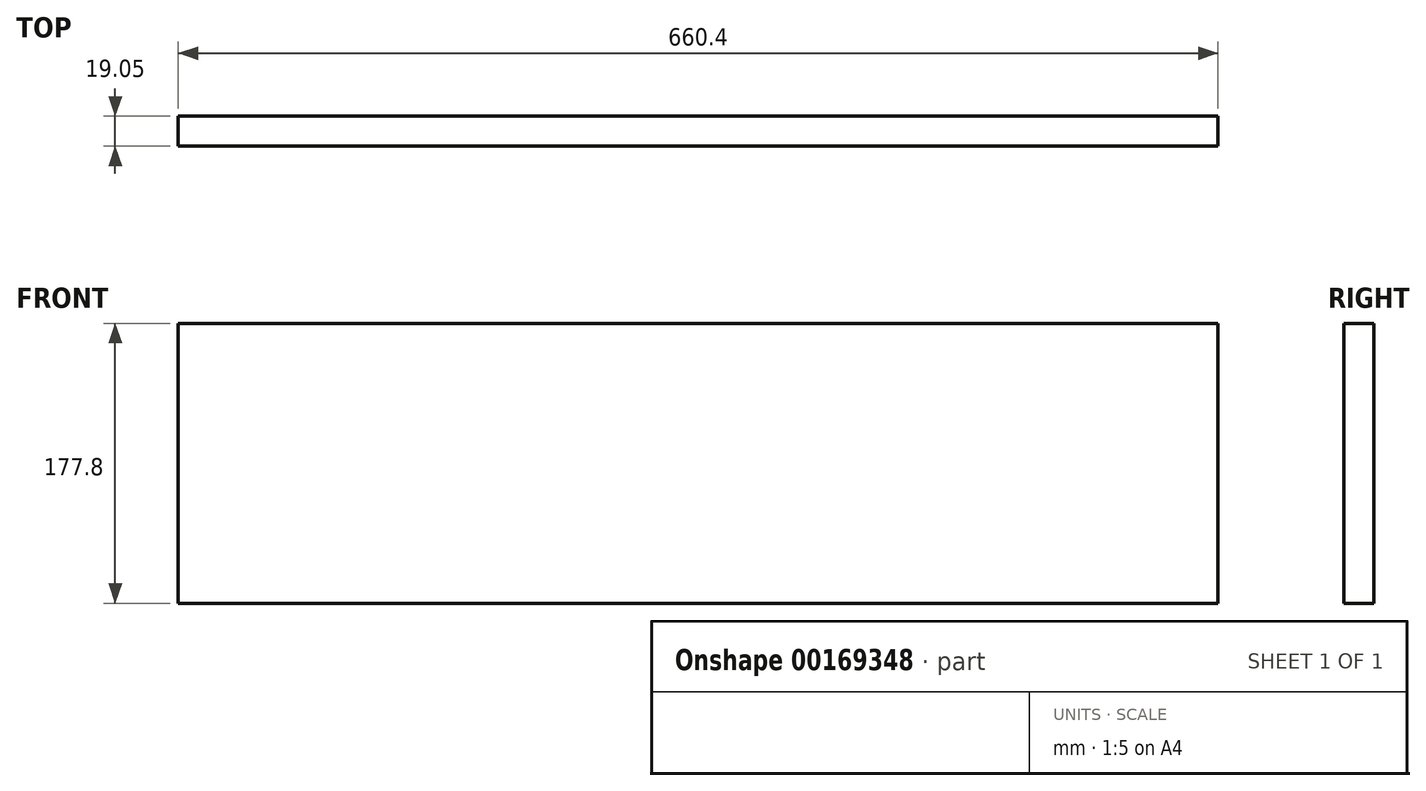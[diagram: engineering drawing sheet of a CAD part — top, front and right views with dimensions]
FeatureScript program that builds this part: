
annotation { "Feature Type Name" : "Feature", "Feature Type Description" : "" }
export const myFeature = defineFeature(function(context is Context, id is Id, definition is map)
    precondition{}
    {
        {
            var Q0;
            Q0=qCreatedBy(makeId("Front.planeOp"),FACE);
            var sketch = newSketch(context, id + "F0", { "sketchPlane" : qUnion([Q0])});
            skLineSegment(sketch, "E0.bottom", {"start": v(0, 0) * mm, "end": v(660.4, 0) * mm});
            skLineSegment(sketch, "E0.top", {"start": v(0, 44.45) * mm, "end": v(660.4, 44.45) * mm});
            skLineSegment(sketch, "E0.left", {"start": v(0, 0) * mm, "end": v(0, 44.45) * mm});
            skLineSegment(sketch, "E0.right", {"start": v(660.4, 0) * mm, "end": v(660.4, 44.45) * mm});
            skLineSegment(sketch, "E1.top", {"start": v(0, 88.9) * mm, "end": v(660.4, 88.9) * mm});
            skLineSegment(sketch, "E1.left", {"start": v(0, 44.45) * mm, "end": v(0, 88.9) * mm});
            skLineSegment(sketch, "E1.right", {"start": v(660.4, 44.45) * mm, "end": v(660.4, 88.9) * mm});
            skLineSegment(sketch, "E2.top", {"start": v(0, 133.35) * mm, "end": v(660.4, 133.35) * mm});
            skLineSegment(sketch, "E2.left", {"start": v(0, 88.9) * mm, "end": v(0, 133.35) * mm});
            skLineSegment(sketch, "E2.right", {"start": v(660.4, 88.9) * mm, "end": v(660.4, 133.35) * mm});
            skLineSegment(sketch, "E3.top", {"start": v(0, 177.8) * mm, "end": v(660.4, 177.8) * mm});
            skLineSegment(sketch, "E3.left", {"start": v(0, 133.35) * mm, "end": v(0, 177.8) * mm});
            skLineSegment(sketch, "E3.right", {"start": v(660.4, 133.35) * mm, "end": v(660.4, 177.8) * mm});
            skSolve(sketch);
        }
        {
            var Q0;
            Q0=makeQuery(id+"F0.imprint","IMPRINT",FACE,{"disambiguationData":[TD([[makeQuery(id+"F0.imprint","IMPRINT",EDGE,{"derivedFrom":sQuery(id+"F0.wireOp",EDGE,"E2.top")}),1.0]])]});
            var Q1;
            Q1=makeQuery(id+"F0.imprint","IMPRINT",FACE,{"disambiguationData":[TD([[makeQuery(id+"F0.imprint","IMPRINT",EDGE,{"derivedFrom":sQuery(id+"F0.wireOp",EDGE,"E1.top")}),1.0]])]});
            var Q2;
            Q2=makeQuery(id+"F0.imprint","IMPRINT",FACE,{"disambiguationData":[TD([[makeQuery(id+"F0.imprint","IMPRINT",EDGE,{"derivedFrom":sQuery(id+"F0.wireOp",EDGE,"E0.top")}),1.0]])]});
            var Q3;
            Q3=makeQuery(id+"F0.imprint","IMPRINT",FACE,{"disambiguationData":[TD([[makeQuery(id+"F0.imprint","IMPRINT",EDGE,{"derivedFrom":sQuery(id+"F0.wireOp",EDGE,"E0.bottom")}),1.0]])]});
            extrude(context, id + "F1", {"entities" : qUnion([Q0, Q1, Q2, Q3]), "oppositeDirection" : true, "depth" : 19.05 * mm});
        }
    });
